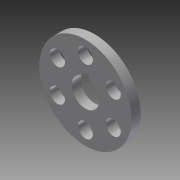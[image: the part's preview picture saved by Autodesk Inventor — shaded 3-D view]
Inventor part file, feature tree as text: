
AUTODESK INVENTOR PART (.ipt)
format: ipt  version: 2013 (Build 170138000, 138)  size: 107,008 bytes
history: native  units: in
note: dims shown in document units (in); Inventor stores cm internally (conversion verified against a paired STEP export)
features: extrude x1, sketch x1
ambient origin geometry x8: Origin, YZ Plane, XZ Plane, XY Plane, X Axis, Y Axis, Z Axis, Center Point
bodies: Solid1 (feature_tree)
feature tree (2):
  extrude  "Extrusion1"  Depth=1.25in
  sketch  "Sketch1"  dims[d0=0.375in d1=1.25in d2=0.25in d3=0.204in d4=2.3622in d6=360.0deg d8=0.125in d9=0.0in d10=0.0469in d11=0.0469in d12=0.0469in]
